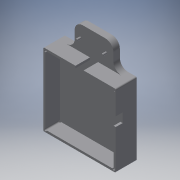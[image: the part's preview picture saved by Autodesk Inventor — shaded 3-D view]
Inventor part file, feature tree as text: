
AUTODESK INVENTOR PART (.ipt)
format: ipt  version: 2019 (Build 230136000, 136)  size: 209,920 bytes
history: native  units: mm
features: extrude x8, sketch x6, projected_geometry x4, fillet x2
ambient origin geometry x8: Origin, YZ Plane, XZ Plane, XY Plane, X Axis, Y Axis, Z Axis, Center Point
bodies: Solid1 (feature_tree)
feature tree (20):
  sketch  "Sketch1"  dims[d0=84.5mm d1=84.5mm]
  extrude  "Extrusion1"  Depth=84.5mm
  extrude  "Extrusion2"  Depth=90.0mm
  extrude  "Extrusion3"  Depth=8.0mm TaperAngle=0.0deg
  extrude  "Extrusion4"  Depth=3.0mm
  extrude  "Extrusion5"  Depth=3.0mm
  sketch  "Sketch5"  dims[d10=3.0mm d11=3.0mm]
  extrude  "Extrusion6"  Depth=10.0mm
  extrude  "Extrusion7"  Depth=11.5mm
  fillet  "Fillet1"  Radius=25.0mm
  fillet  "Fillet2"  Radius=9.5mm
  extrude  "Extrusion8"  Depth=10.0mm TaperAngle=0.0deg
  sketch  "Sketch2"  dims[d2=90.0mm d3=90.0mm]
  projected_geometry  "Projected Loop1"
  sketch  "Sketch3"  dims[d4=18.0mm d5=0.0mm d6=8.0mm d7=0.0mm]
  projected_geometry  "Projected Loop2"
  sketch  "Sketch4"  dims[d8=3.0mm d9=3.0mm]
  projected_geometry  "Projected Loop3"
  projected_geometry  "Projected Loop4"
  sketch  "Sketch6"  dims[d12=10.0mm d13=0.0mm d14=10.0mm d15=11.5mm d16=25.0mm d17=9.5mm d18=10.0mm d19=0.0mm d22=10.0mm d23=10.0mm d24=0.0mm d25=48.0mm d26=30.0mm d27=2.6mm d28=2.6mm d29=32.0mm d30=10.0mm d31=0.0mm d32=5.0mm d33=0.0mm d34=10.0mm d35=1.5mm d37=12.2mm d38=12.2mm d39=12.2mm d40=12.2mm d41=40.0mm d42=1.6mm d43=0.0mm]
